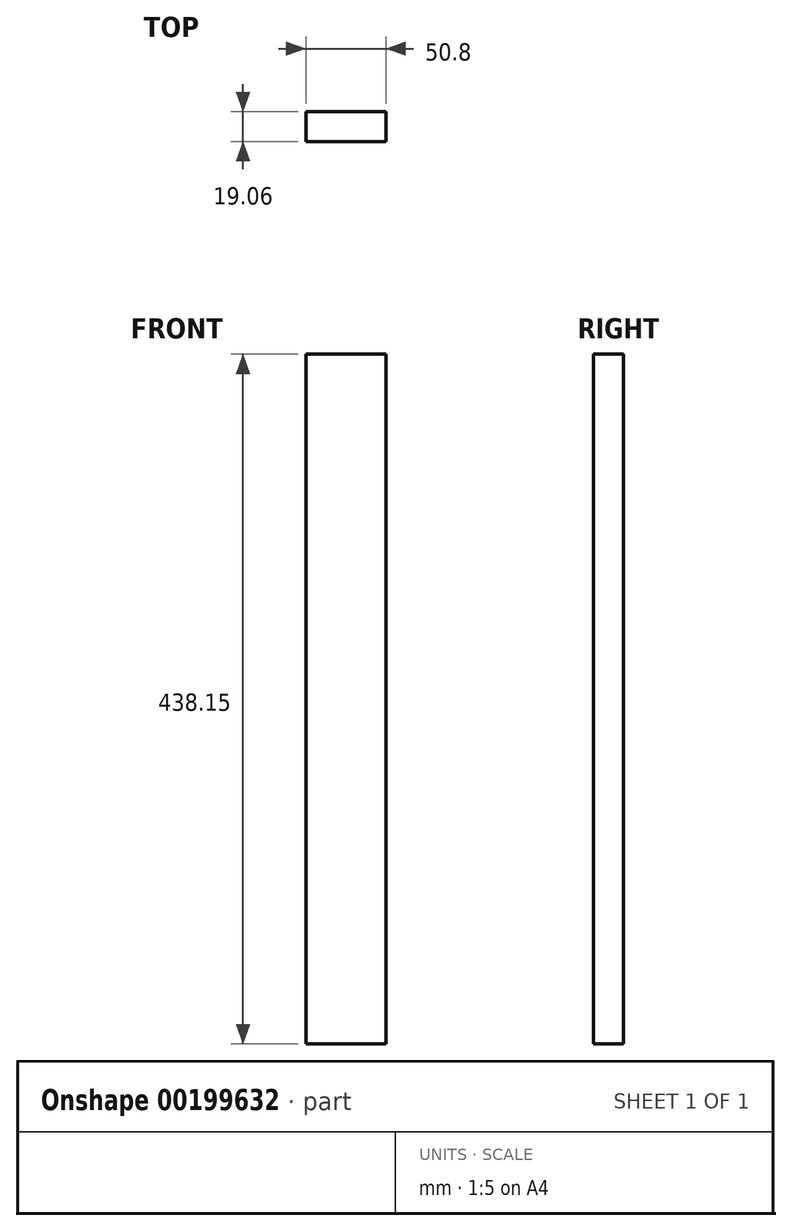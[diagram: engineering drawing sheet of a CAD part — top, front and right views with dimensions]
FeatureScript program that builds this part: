
annotation { "Feature Type Name" : "Feature", "Feature Type Description" : "" }
export const myFeature = defineFeature(function(context is Context, id is Id, definition is map)
    precondition{}
    {
        {
            var Q0;
            Q0=qCreatedBy(makeId("Front.planeOp"),FACE);
            var sketch = newSketch(context, id + "F0", { "sketchPlane" : qUnion([Q0])});
            skLineSegment(sketch, "E0.bottom", {"start": v(-72.07, 144.76) * mm, "end": v(-21.27, 144.76) * mm});
            skLineSegment(sketch, "E0.top", {"start": v(-72.07, -293.39) * mm, "end": v(-21.27, -293.39) * mm});
            skLineSegment(sketch, "E0.left", {"start": v(-72.07, 144.76) * mm, "end": v(-72.07, -293.39) * mm});
            skLineSegment(sketch, "E0.right", {"start": v(-21.27, 144.76) * mm, "end": v(-21.27, -293.39) * mm});
            skSolve(sketch);
        }
        {
            var Q0;
            Q0=makeQuery(id+"F0.imprint","IMPRINT",FACE,{"disambiguationData":[TD([[makeQuery(id+"F0.imprint","IMPRINT",EDGE,{"derivedFrom":sQuery(id+"F0.wireOp",EDGE,"E0.bottom")}),-1.0]])]});
            extrude(context, id + "F1", {"entities" : qUnion([Q0]), "endBound" : BoundingType.SYMMETRIC, "depth" : 19.05 * mm});
        }
    });
